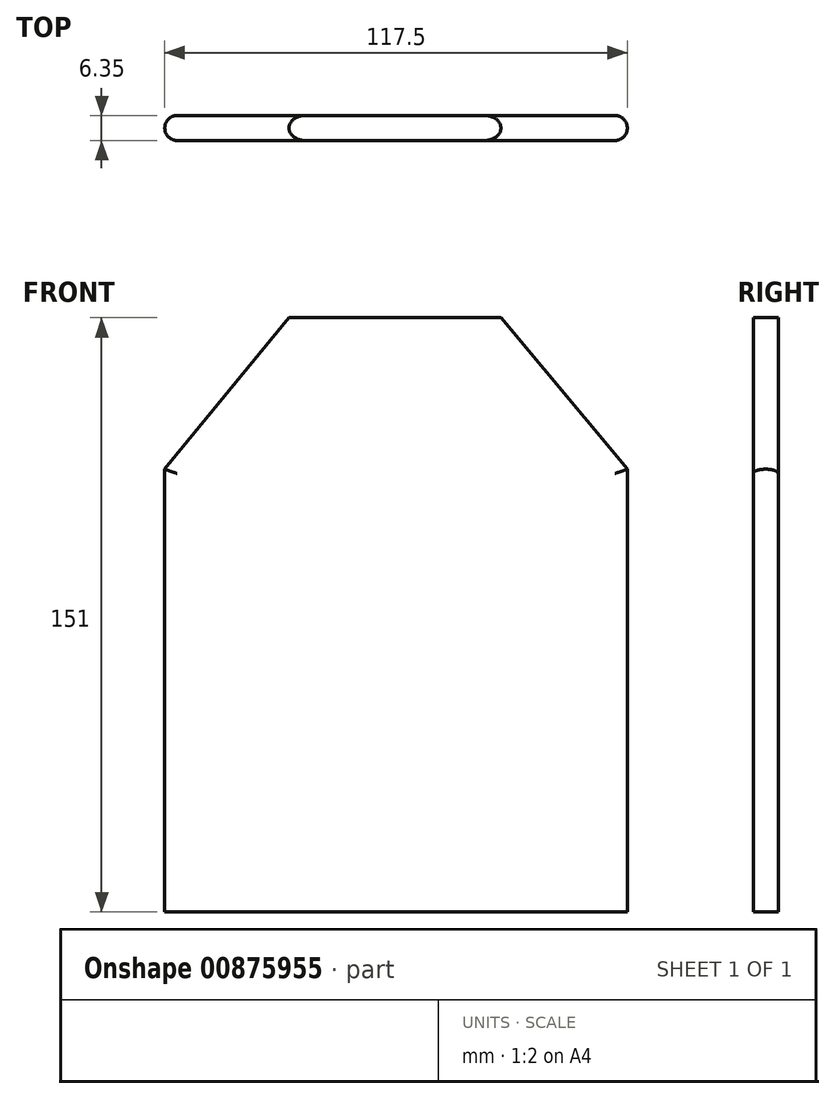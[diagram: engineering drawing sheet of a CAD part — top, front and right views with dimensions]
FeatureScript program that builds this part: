
annotation { "Feature Type Name" : "Feature", "Feature Type Description" : "" }
export const myFeature = defineFeature(function(context is Context, id is Id, definition is map)
    precondition{}
    {
        {
            var Q0;
            Q0=qCreatedBy(makeId("Front.planeOp"),FACE);
            var sketch = newSketch(context, id + "F0", { "sketchPlane" : qUnion([Q0])});
            skLineSegment(sketch, "E0.bottom", {"start": v(-54.43, 88.53) * mm, "end": v(63.07, 88.53) * mm});
            skLineSegment(sketch, "E0.top", {"start": v(-54.43, -62.47) * mm, "end": v(63.07, -62.47) * mm});
            skLineSegment(sketch, "E0.left", {"start": v(-54.43, 88.53) * mm, "end": v(-54.43, -62.47) * mm});
            skLineSegment(sketch, "E0.right", {"start": v(63.07, 88.53) * mm, "end": v(63.07, -62.47) * mm});
            skLineSegment(sketch, "E1", {"start": v(-54.43, 50.03) * mm, "end": v(-22.85, 88.53) * mm});
            skLineSegment(sketch, "E2", {"start": v(-22.85, 88.53) * mm, "end": v(30.95, 88.53) * mm});
            skLineSegment(sketch, "E3", {"start": v(30.95, 88.53) * mm, "end": v(63.07, 50.03) * mm});
            skSolve(sketch);
        }
        {
            var Q0;
            {var subQ1=sQuery(id+"F0.wireOp",EDGE,"E0.top");Q0=makeQuery(id+"F0.imprint","IMPRINT",FACE,{"disambiguationData":[TD([[makeQuery(id+"F0.imprint","IMPRINT",EDGE,{"derivedFrom":subQ1}),1.0]])]});}
            extrude(context, id + "F1", {"entities" : qUnion([Q0]), "depth" : 6.35 * mm, "offsetDistance" : 25.4 * mm});
        }
        {
            var Q0;
            Q0=makeQuery(id+"F1.opExtrude","CAP_EDGE",EDGE,{"disambiguationData":[OSD([sQuery(id+"F0.wireOp",EDGE,"E0.left")])],"isStart":true});
            var Q1;
            Q1=makeQuery(id+"F1.opExtrude","CAP_EDGE",EDGE,{"disambiguationData":[OSD([sQuery(id+"F0.wireOp",EDGE,"E1")])],"isStart":true});
            var Q2;
            Q2=makeQuery(id+"F1.opExtrude","CAP_EDGE",EDGE,{"disambiguationData":[OSD([sQuery(id+"F0.wireOp",EDGE,"E3")])],"isStart":true});
            var Q3;
            Q3=makeQuery(id+"F1.opExtrude","CAP_EDGE",EDGE,{"disambiguationData":[OSD([sQuery(id+"F0.wireOp",EDGE,"E0.right")])],"isStart":true});
            var Q4;
            Q4=makeQuery(id+"F1.opExtrude","CAP_EDGE",EDGE,{"disambiguationData":[OSD([sQuery(id+"F0.wireOp",EDGE,"E3")])],"isStart":false});
            var Q5;
            Q5=makeQuery(id+"F1.opExtrude","CAP_EDGE",EDGE,{"disambiguationData":[OSD([sQuery(id+"F0.wireOp",EDGE,"E1")])],"isStart":false});
            var Q6;
            Q6=makeQuery(id+"F1.opExtrude","CAP_EDGE",EDGE,{"disambiguationData":[OSD([sQuery(id+"F0.wireOp",EDGE,"E0.left")])],"isStart":false});
            var Q7;
            Q7=makeQuery(id+"F1.opExtrude","CAP_EDGE",EDGE,{"disambiguationData":[OSD([sQuery(id+"F0.wireOp",EDGE,"E0.right")])],"isStart":false});
            fillet(context, id + "F2", {"entities" : qUnion([Q0, Q1, Q2, Q3, Q4, Q5, Q6, Q7]), "radius" : 3.12 * mm, "tangentPropagation" : true, "allowEdgeOverflow" : false});
        }
    });
